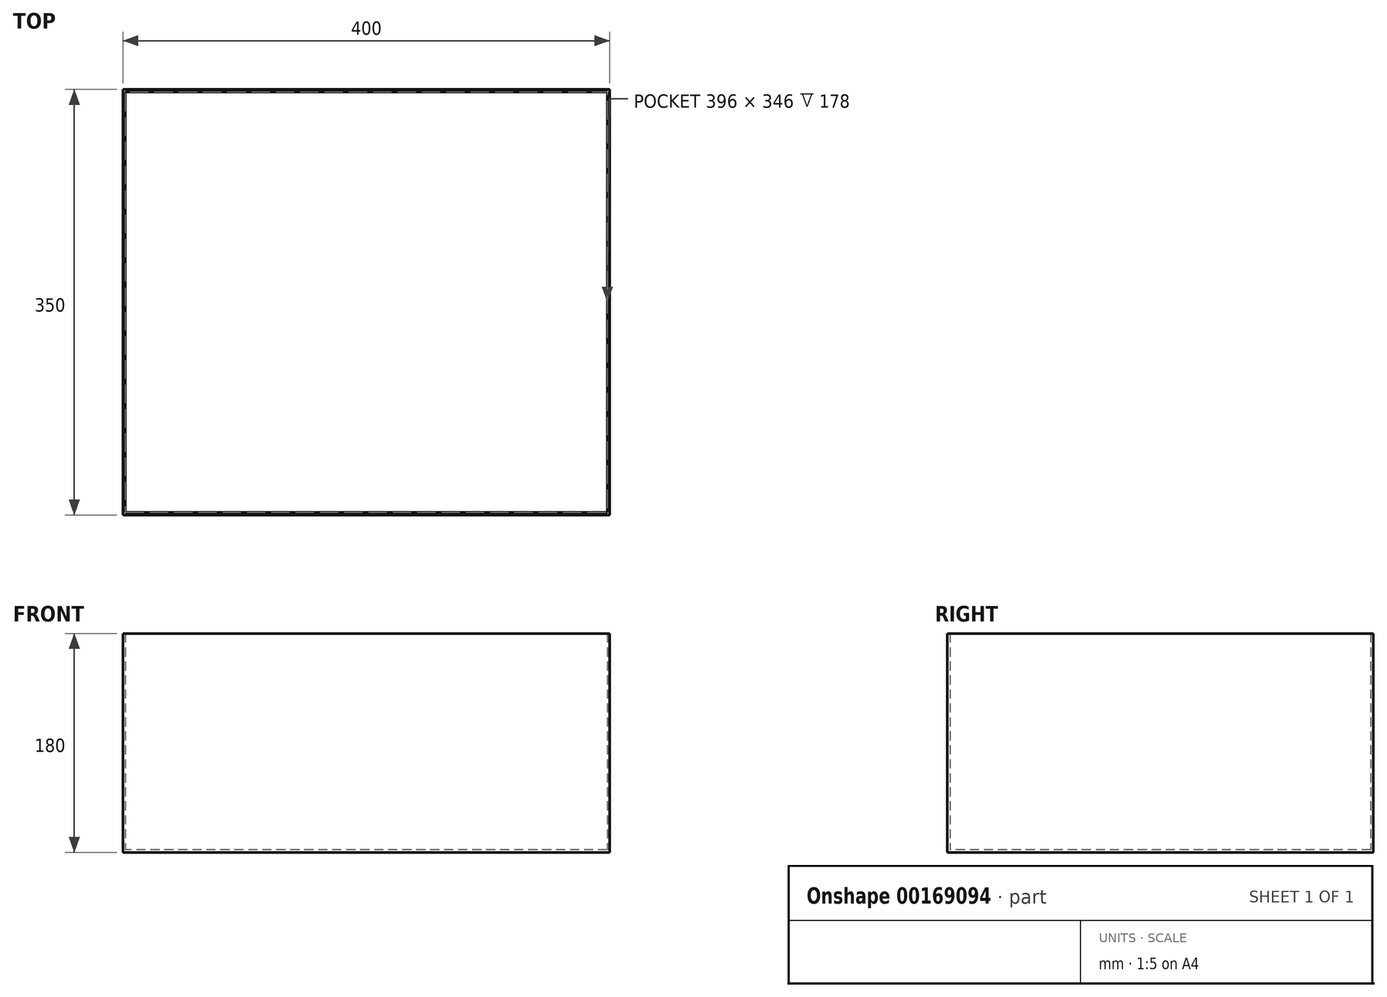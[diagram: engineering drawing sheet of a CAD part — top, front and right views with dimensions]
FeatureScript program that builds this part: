
annotation { "Feature Type Name" : "Feature", "Feature Type Description" : "" }
export const myFeature = defineFeature(function(context is Context, id is Id, definition is map)
    precondition{}
    {
        {
            var Q0;
            Q0=qCreatedBy(makeId("Top.planeOp"),FACE);
            var sketch = newSketch(context, id + "F0", { "sketchPlane" : qUnion([Q0])});
            skLineSegment(sketch, "E0.bottom", {"start": v(200, -175) * mm, "end": v(-200, -175) * mm});
            skLineSegment(sketch, "E0.top", {"start": v(200, 175) * mm, "end": v(-200, 175) * mm});
            skLineSegment(sketch, "E0.left", {"start": v(200, -175) * mm, "end": v(200, 175) * mm});
            skLineSegment(sketch, "E0.right", {"start": v(-200, -175) * mm, "end": v(-200, 175) * mm});
            skPoint(sketch, "E0.middle", {"position": v(0, 0) * mm});
            skLineSegment(sketch, "E1.bottom", {"start": v(198, 173) * mm, "end": v(-198, 173) * mm});
            skLineSegment(sketch, "E1.top", {"start": v(198, -173) * mm, "end": v(-198, -173) * mm});
            skLineSegment(sketch, "E1.left", {"start": v(198, 173) * mm, "end": v(198, -173) * mm});
            skLineSegment(sketch, "E1.right", {"start": v(-198, 173) * mm, "end": v(-198, -173) * mm});
            skSolve(sketch);
        }
        {
            var Q0;
            Q0 = qSketchRegion(id + "F0", true);
            extrude(context, id + "F1", {"entities" : qUnion([Q0]), "depth" : 180 * mm});
        }
        {
            var Q0;
            Q0=makeQuery(id+"F0.imprint","IMPRINT",FACE,{"disambiguationData":[TD([[makeQuery(id+"F0.imprint","IMPRINT",EDGE,{"derivedFrom":sQuery(id+"F0.wireOp",EDGE,"E1.bottom")}),1.0]])]});
            extrude(context, id + "F2", {"entities" : qUnion([Q0]), "operationType" : NewBodyOperationType.ADD, "depth" : 2 * mm});
        }
    });
